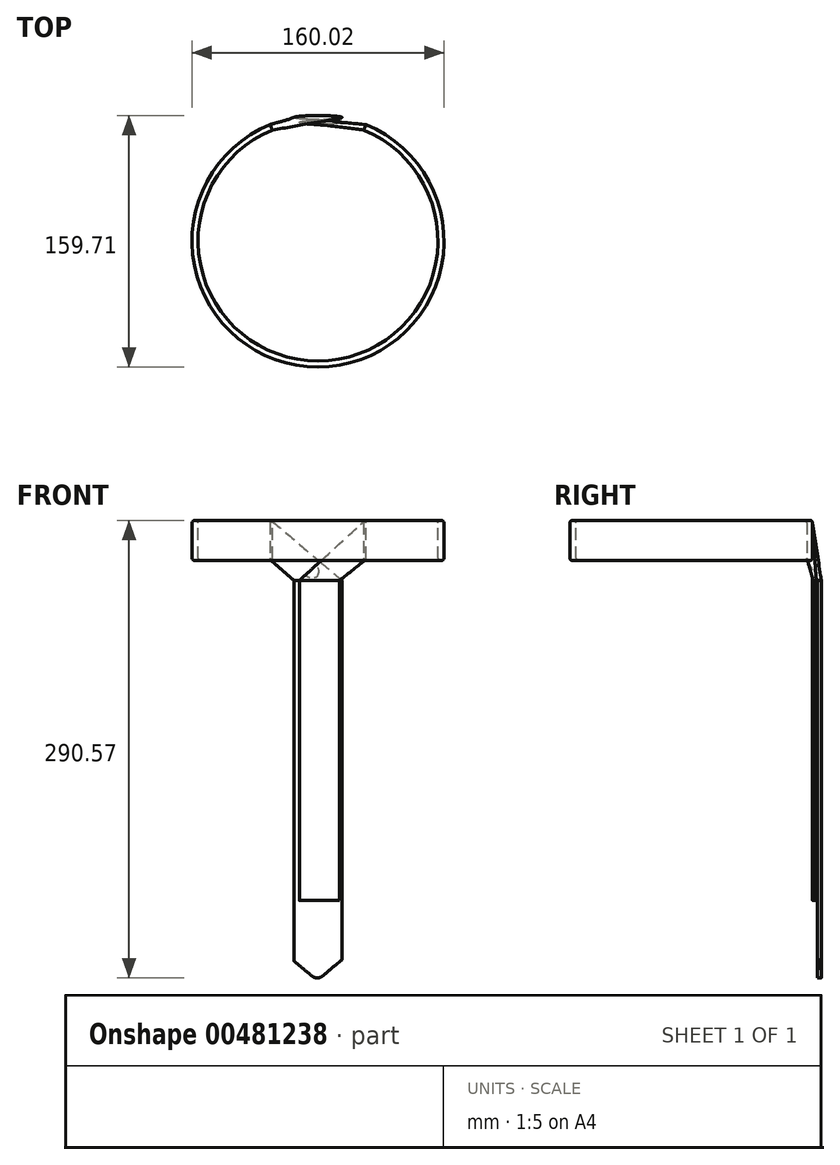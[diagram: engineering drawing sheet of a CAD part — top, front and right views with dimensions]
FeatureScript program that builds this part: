
annotation { "Feature Type Name" : "Feature", "Feature Type Description" : "" }
export const myFeature = defineFeature(function(context is Context, id is Id, definition is map)
    precondition{}
    {
        {
            var Q0;
            Q0=qCreatedBy(makeId("Front.planeOp"),FACE);
            var sketch = newSketch(context, id + "F0", { "sketchPlane" : qUnion([Q0])});
            skLineSegment(sketch, "E0.bottom", {"start": v(78.49, -12.7) * mm, "end": v(77.72, -12.7) * mm});
            skLineSegment(sketch, "E0.top", {"start": v(78.49, 12.7) * mm, "end": v(77.72, 12.7) * mm});
            skLineSegment(sketch, "E0.left", {"start": v(80, -11.18) * mm, "end": v(80, 11.18) * mm});
            skLineSegment(sketch, "E0.right", {"start": v(76.2, -11.18) * mm, "end": v(76.2, 11.18) * mm});
            skPoint(sketch, "E0.middle", {"position": v(78.1, 0) * mm});
            skPoint(sketch, "E1.visualSharp", {"position": v(76.2, 12.7) * mm});
            skArc(sketch, "E1.filletArc", {"start": v(77.72, 12.7) * mm, "mid": v(76.65, 12.25) * mm, "end": v(76.2, 11.18) * mm});
            skPoint(sketch, "E2.visualSharp", {"position": v(80, 12.7) * mm});
            skArc(sketch, "E2.filletArc", {"start": v(80, 11.18) * mm, "mid": v(79.56, 12.25) * mm, "end": v(78.49, 12.7) * mm});
            skPoint(sketch, "E3.visualSharp", {"position": v(80, -12.7) * mm});
            skArc(sketch, "E3.filletArc", {"start": v(78.49, -12.7) * mm, "mid": v(79.56, -12.25) * mm, "end": v(80, -11.18) * mm});
            skPoint(sketch, "E4.visualSharp", {"position": v(76.2, -12.7) * mm});
            skArc(sketch, "E4.filletArc", {"start": v(76.2, -11.18) * mm, "mid": v(76.65, -12.25) * mm, "end": v(77.72, -12.7) * mm});
            skLineSegment(sketch, "E5", {"start": v(0, 0) * mm, "end": v(0, -94.05) * mm, "construction": true});
            skSolve(sketch);
        }
        {
            var Q0;
            Q0=makeQuery(id+"F0.imprint","IMPRINT",FACE,{"disambiguationData":[TD([[makeQuery(id+"F0.imprint","IMPRINT",EDGE,{"derivedFrom":sQuery(id+"F0.wireOp",EDGE,"E0.bottom")}),-1.0]])]});
            var Q1;
            Q1 = qConstructionFilter(qBodyType(qCreatedBy(id + "F0" ,EDGE), BodyType.WIRE), ConstructionObject.NO);
            var Q2;
            Q2=sQuery(id+"F0.wireOp",EDGE,"E5");
            revolve(context, id + "F1", {"entities" : qUnion([Q0]), "surfaceEntities" : qUnion([Q1]), "axis" : qUnion([Q2]), "revolveType" : RevolveType.FULL});
        }
        {
            var Q0;
            Q0=qCreatedBy(makeId("Top.planeOp"),FACE);
            var sketch = newSketch(context, id + "F2", { "sketchPlane" : qUnion([Q0])});
            skLineSegment(sketch, "E6", {"start": v(0, 0) * mm, "end": v(36.97, 89.83) * mm});
            skLineSegment(sketch, "E7", {"start": v(36.97, 89.83) * mm, "end": v(-36.97, 89.83) * mm});
            skLineSegment(sketch, "E8", {"start": v(0, 0) * mm, "end": v(0, 109.14) * mm, "construction": true});
            skLineSegment(sketch, "E9.MirrorCS", {"start": v(0, 0) * mm, "end": v(-36.97, 89.83) * mm});
            skSolve(sketch);
        }
        {
            var Q0;
            Q0 = qSketchRegion(id + "F2", true);
            extrude(context, id + "F3", {"entities" : qUnion([Q0]), "operationType" : NewBodyOperationType.REMOVE, "endBound" : BoundingType.SYMMETRIC, "depth" : 76.2 * mm});
        }
        {
            var Q0;
            Q0=makeQuery(id+"F1.opRevolve","SWEPT_FACE",FACE,{"disambiguationData":[OSD([sQuery(id+"F0.wireOp",EDGE,"E0.bottom")])]});
            cPlane(context, id + "F4", {"entities" : qUnion([Q0]), "cplaneType" : CPlaneType.OFFSET, "offset" : 12.7 * mm, "width" : 152.4 * mm, "height" : 152.4 * mm});
        }
        {
            var Q0;
            Q0=qCreatedBy(id+"F4.planeOp",FACE);
            var sketch = newSketch(context, id + "F5", { "sketchPlane" : qUnion([Q0])});
            skEllipse(sketch, "E10", {"center": v(0, -78.43) * mm, "majorRadius": 15.24 * mm, "minorRadius": 1.27 * mm, "majorAxis": v(1, 0)});
            skSolve(sketch);
        }
        {
            var Q1;
            Q1=makeQuery(id+"F3.boolean.opBoolean","COPY",FACE,{"derivedFrom":makeQuery(id+"F3.opExtrude","SWEPT_FACE",FACE,{"disambiguationData":[OSD([sQuery(id+"F2.wireOp",EDGE,"E9.MirrorCS")])]})});
            var Q2;
            Q2=makeQuery(id+"F5.imprint","IMPRINT",FACE,{"disambiguationData":[TD([[makeQuery(id+"F5.imprint","IMPRINT",EDGE,{"derivedFrom":sQuery(id+"F5.wireOp",EDGE,"E10")}),1.0]])]});
            loft(context, id + "F6", {"operationType" : NewBodyOperationType.ADD, "sheetProfilesArray" : [{ "sheetProfileEntities" : qUnion([Q1]) }, { "sheetProfileEntities" : qUnion([Q2]) }]});
        }
        {
            var Q0;
            Q0=makeQuery(id+"F6.opLoft","CAP_FACE",FACE,{"disambiguationData":[OSD([makeQuery(id+"F5.imprint","IMPRINT",FACE,{"disambiguationData":[TD([[makeQuery(id+"F5.imprint","IMPRINT",EDGE,{"derivedFrom":sQuery(id+"F5.wireOp",EDGE,"E10")}),1.0]])]})])],"isStart":true});
            extrude(context, id + "F7", {"entities" : qUnion([Q0]), "operationType" : NewBodyOperationType.ADD, "depth" : 254 * mm});
        }
        {
            var Q0;
            Q0=qCreatedBy(id+"F4.planeOp",FACE);
            var sketch = newSketch(context, id + "F8", { "sketchPlane" : qUnion([Q0])});
            skEllipse(sketch, "E11", {"center": v(0.88, -75.37) * mm, "majorRadius": 12.7 * mm, "minorRadius": 1.27 * mm, "majorAxis": v(1, 0)});
            skSolve(sketch);
        }
        {
            var Q1;
            Q1=makeQuery(id+"F8.imprint","IMPRINT",FACE,{"disambiguationData":[TD([[makeQuery(id+"F8.imprint","IMPRINT",EDGE,{"derivedFrom":sQuery(id+"F8.wireOp",EDGE,"E11")}),1.0]])]});
            var Q2;
            Q2=makeQuery(id+"F3.boolean.opBoolean","COPY",FACE,{"derivedFrom":makeQuery(id+"F3.opExtrude","SWEPT_FACE",FACE,{"disambiguationData":[OSD([sQuery(id+"F2.wireOp",EDGE,"E6")])]})});
            loft(context, id + "F9", {"operationType" : NewBodyOperationType.ADD, "sheetProfilesArray" : [{ "sheetProfileEntities" : qUnion([Q1]) }, { "sheetProfileEntities" : qUnion([Q2]) }]});
        }
        {
            var Q0;
            Q0=makeQuery(id+"F9.opLoft","CAP_FACE",FACE,{"disambiguationData":[OSD([makeQuery(id+"F8.imprint","IMPRINT",FACE,{"disambiguationData":[TD([[makeQuery(id+"F8.imprint","IMPRINT",EDGE,{"derivedFrom":sQuery(id+"F8.wireOp",EDGE,"E11")}),1.0]])]})])],"isStart":true});
            extrude(context, id + "F10", {"entities" : qUnion([Q0]), "operationType" : NewBodyOperationType.ADD, "depth" : 203.2 * mm});
        }
        {
            var Q0;
            Q0=qCreatedBy(makeId("Front.planeOp"),FACE);
            cPlane(context, id + "F11", {"entities" : qUnion([Q0]), "cplaneType" : CPlaneType.OFFSET, "offset" : 77.01 * mm, "oppositeDirection" : true, "width" : 152.4 * mm, "height" : 152.4 * mm});
        }
        {
            var Q0;
            Q0=qCreatedBy(id+"F11.planeOp",FACE);
            var sketch = newSketch(context, id + "F12", { "sketchPlane" : qUnion([Q0])});
            skLineSegment(sketch, "E12", {"start": v(-18.4, -264.52) * mm, "end": v(-18.4, -291.08) * mm});
            skLineSegment(sketch, "E13", {"start": v(-0.5, -279.4) * mm, "end": v(-18.4, -264.52) * mm});
            skLineSegment(sketch, "E14", {"start": v(-0.5, -279.4) * mm, "end": v(-0.5, -263.23) * mm, "construction": true});
            skLineSegment(sketch, "E15.MirrorCS", {"start": v(-0.5, -279.4) * mm, "end": v(17.38, -264.52) * mm});
            skLineSegment(sketch, "E16.MirrorCS", {"start": v(17.38, -264.52) * mm, "end": v(17.38, -291.08) * mm});
            skLineSegment(sketch, "E17", {"start": v(17.38, -291.08) * mm, "end": v(-18.4, -291.08) * mm});
            skSolve(sketch);
        }
        {
            var Q0;
            Q0 = qSketchRegion(id + "F12", true);
            extrude(context, id + "F13", {"entities" : qUnion([Q0]), "operationType" : NewBodyOperationType.REMOVE, "endBound" : BoundingType.SYMMETRIC, "depth" : 25.4 * mm});
        }
        {
            var Q0;
            Q0=makeQuery(id+"F13.boolean.opBoolean","COPY",EDGE,{"derivedFrom":makeQuery(id+"F13.opExtrude","SWEPT_EDGE",EDGE,{"disambiguationData":[OSD([sQuery(id+"F12.wireOp",EDGE,"E13"),sQuery(id+"F12.wireOp",EDGE,"E15.MirrorCS")])]})});
            fillet(context, id + "F14", {"entities" : qUnion([Q0]), "radius" : 5.08 * mm, "tangentPropagation" : true, "allowEdgeOverflow" : false});
        }
    });
